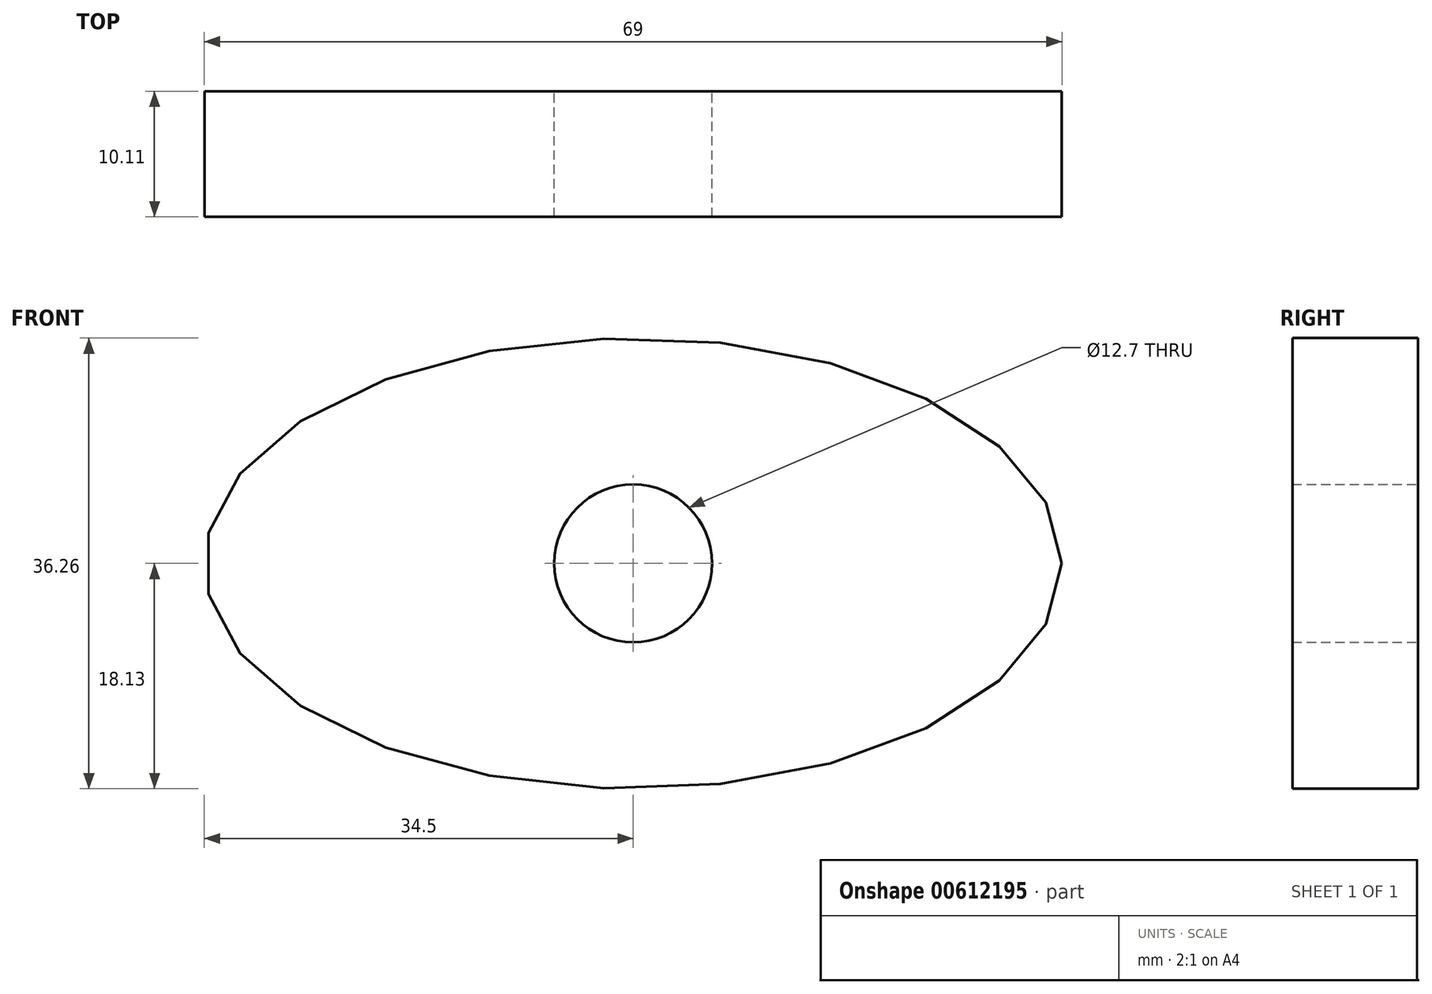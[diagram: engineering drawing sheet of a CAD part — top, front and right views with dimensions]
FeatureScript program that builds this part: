
annotation { "Feature Type Name" : "Feature", "Feature Type Description" : "" }
export const myFeature = defineFeature(function(context is Context, id is Id, definition is map)
    precondition{}
    {
        {
            var Q0;
            Q0=qCreatedBy(makeId("Front.planeOp"),FACE);
            var sketch = newSketch(context, id + "F0", { "sketchPlane" : qUnion([Q0])});
            skEllipse(sketch, "E0", {"center": v(0, 0) * mm, "majorRadius": 34.5 * mm, "minorRadius": 18.13 * mm, "majorAxis": v(1, 0)});
            skSolve(sketch);
        }
        {
            var Q0;
            Q0 = qSketchRegion(id + "F0", true);
            var Q1;
            Q1 = qSketchRegion(id + "F0", true);
            var Q2;
            Q2 = qSketchRegion(id + "F0", true);
            extrude(context, id + "F1", {"entities" : qUnion([Q0, Q1, Q2]), "depth" : 10.1 * mm, "offsetDistance" : 25.4 * mm});
        }
        {
            var Q0;
            Q0=sQuery(id+"F0.wireOp",VERTEX,"E0.center");
            var Q1;
            Q1=makeQuery(id+"F1.opExtrude","SWEPT_BODY",BODY,{"disambiguationData":[OSD([sQuery(id+"F0.wireOp",EDGE,"E0")])]});
            hole(context, id + "F2", {"style" : HoleStyle.SIMPLE, "endStyle" : HoleEndStyle.THROUGH, "oppositeDirection" : true, "holeDiameter" : 12.7 * mm, "majorDiameter" : 6.35 * mm, "isTappedThrough" : true, "tappedDepth" : 12.7 * mm, "tapClearance" : 3, "locations" : qUnion([Q0]), "scope" : qUnion([Q1])});
        }
    });
